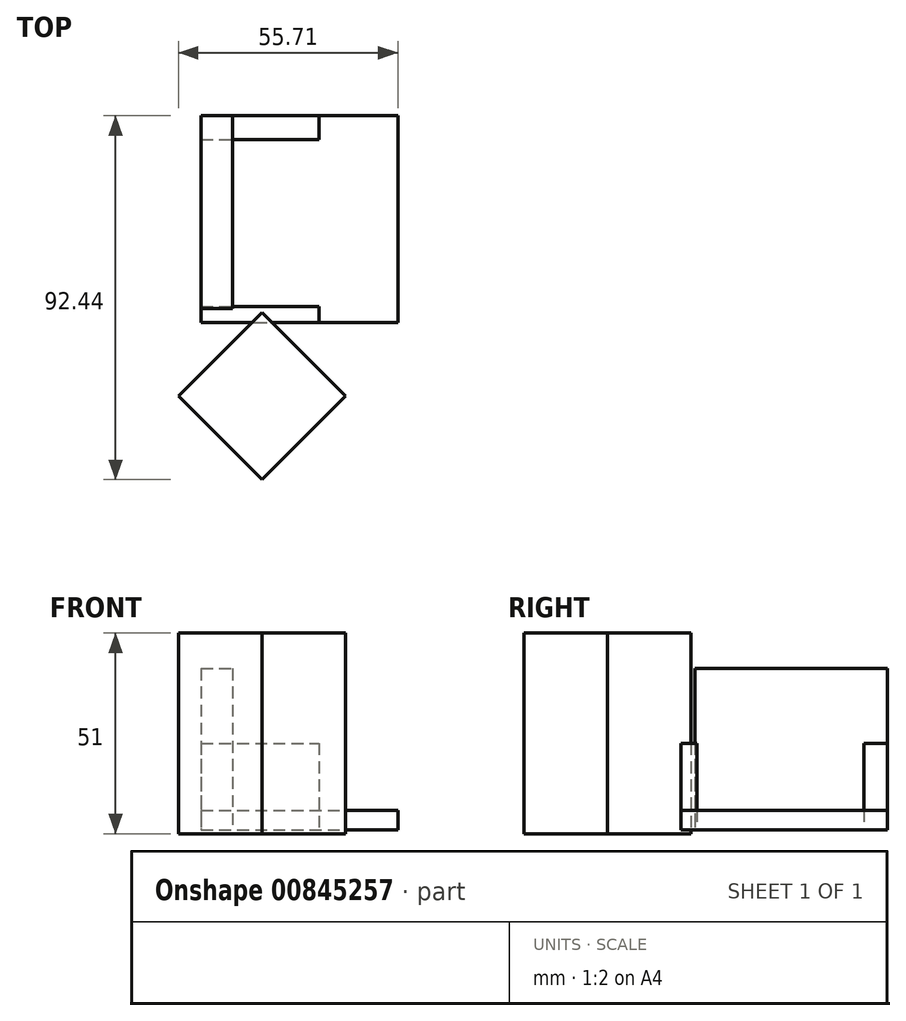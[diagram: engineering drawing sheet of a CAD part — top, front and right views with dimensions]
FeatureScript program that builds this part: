
annotation { "Feature Type Name" : "Feature", "Feature Type Description" : "" }
export const myFeature = defineFeature(function(context is Context, id is Id, definition is map)
    precondition{}
    {
        {
            var Q0;
            Q0=qCreatedBy(makeId("Top.planeOp"),FACE);
            var sketch = newSketch(context, id + "F0", { "sketchPlane" : qUnion([Q0])});
            skLineSegment(sketch, "E0.bottom", {"start": v(0, 0) * mm, "end": v(8, 0) * mm});
            skLineSegment(sketch, "E0.top", {"start": v(0, 49) * mm, "end": v(8, 49) * mm});
            skLineSegment(sketch, "E0.left", {"start": v(0, 0) * mm, "end": v(0, 49) * mm});
            skLineSegment(sketch, "E0.right", {"start": v(8, 0) * mm, "end": v(8, 49) * mm});
            skSolve(sketch);
        }
        {
            var Q0;
            Q0=makeQuery(id+"F0.imprint","IMPRINT",FACE,{"disambiguationData":[TD([[makeQuery(id+"F0.imprint","IMPRINT",EDGE,{"derivedFrom":sQuery(id+"F0.wireOp",EDGE,"E0.bottom")}),1.0]])]});
            extrude(context, id + "F1", {"entities" : qUnion([Q0]), "depth" : (16 + 25) * mm, "offsetDistance" : 25 * mm});
        }
        {
            var Q0;
            Q0=makeQuery(id+"F1.opExtrude","SWEPT_BODY",BODY,{"disambiguationData":[OSD([sQuery(id+"F0.wireOp",EDGE,"E0.bottom"),sQuery(id+"F0.wireOp",EDGE,"E0.top"),sQuery(id+"F0.wireOp",EDGE,"E0.left"),sQuery(id+"F0.wireOp",EDGE,"E0.right")])]});
            transform(context, id + "F2", {"entities" : qUnion([Q0]), "transformType" : TransformType.TRANSLATION_3D, "dx" : 0 * mm, "dy" : -1.5 * mm, "dz" : 0 * mm, "makeCopy" : false});
        }
        {
            var Q0;
            Q0=qCreatedBy(makeId("Top.planeOp"),FACE);
            var sketch = newSketch(context, id + "F3", { "sketchPlane" : qUnion([Q0])});
            skLineSegment(sketch, "E1.bottom", {"start": v(0, 0) * mm, "end": v(30, 0) * mm});
            skLineSegment(sketch, "E1.top", {"start": v(0, 4) * mm, "end": v(30, 4) * mm});
            skLineSegment(sketch, "E1.left", {"start": v(0, 0) * mm, "end": v(0, 4) * mm});
            skLineSegment(sketch, "E1.right", {"start": v(30, 0) * mm, "end": v(30, 4) * mm});
            skSolve(sketch);
        }
        {
            var Q0;
            Q0 = qSketchRegion(id + "F3", true);
            extrude(context, id + "F4", {"entities" : qUnion([Q0]), "depth" : 22 * mm, "offsetDistance" : 25 * mm});
        }
        {
            var Q0;
            Q0=makeQuery(id+"F4.opExtrude","SWEPT_BODY",BODY,{"disambiguationData":[OSD([sQuery(id+"F3.wireOp",EDGE,"E1.bottom"),sQuery(id+"F3.wireOp",EDGE,"E1.top"),sQuery(id+"F3.wireOp",EDGE,"E1.left"),sQuery(id+"F3.wireOp",EDGE,"E1.right")])]});
            transform(context, id + "F5", {"entities" : qUnion([Q0]), "transformType" : TransformType.TRANSLATION_3D, "dx" : 0 * mm, "dy" : -5 * mm, "dz" : 0 * mm, "makeCopy" : false});
        }
        {
            var Q0;
            Q0=qCreatedBy(makeId("Top.planeOp"),FACE);
            var sketch = newSketch(context, id + "F6", { "sketchPlane" : qUnion([Q0])});
            skLineSegment(sketch, "E2.bottom", {"start": v(0, 0) * mm, "end": v(30, 0) * mm});
            skLineSegment(sketch, "E2.top", {"start": v(0, 6.01) * mm, "end": v(30, 6.01) * mm});
            skLineSegment(sketch, "E2.left", {"start": v(0, 0) * mm, "end": v(0, 6.01) * mm});
            skLineSegment(sketch, "E2.right", {"start": v(30, 0) * mm, "end": v(30, 6.01) * mm});
            skSolve(sketch);
        }
        {
            var Q0;
            Q0 = qSketchRegion(id + "F6", true);
            extrude(context, id + "F7", {"entities" : qUnion([Q0]), "depth" : 22 * mm, "offsetDistance" : 25 * mm});
        }
        {
            var Q0;
            Q0=makeQuery(id+"F7.opExtrude","SWEPT_BODY",BODY,{"disambiguationData":[OSD([sQuery(id+"F6.wireOp",EDGE,"E2.bottom"),sQuery(id+"F6.wireOp",EDGE,"E2.top"),sQuery(id+"F6.wireOp",EDGE,"E2.left"),sQuery(id+"F6.wireOp",EDGE,"E2.right")])]});
            transform(context, id + "F8", {"entities" : qUnion([Q0]), "transformType" : TransformType.TRANSLATION_3D, "dx" : 0 * mm, "dy" : 41.5 * mm, "dz" : 0 * mm, "makeCopy" : false});
        }
        {
            var Q0;
            Q0=qCreatedBy(makeId("Top.planeOp"),FACE);
            var sketch = newSketch(context, id + "F9", { "sketchPlane" : qUnion([Q0])});
            skLineSegment(sketch, "E3.bottom", {"start": v(0, 0) * mm, "end": v(50, 0) * mm});
            skLineSegment(sketch, "E3.top", {"start": v(0, 52.5) * mm, "end": v(50, 52.5) * mm});
            skLineSegment(sketch, "E3.left", {"start": v(0, 0) * mm, "end": v(0, 52.5) * mm});
            skLineSegment(sketch, "E3.right", {"start": v(50, 0) * mm, "end": v(50, 52.5) * mm});
            skSolve(sketch);
        }
        {
            var Q0;
            Q0 = qSketchRegion(id + "F9", true);
            extrude(context, id + "F10", {"entities" : qUnion([Q0]), "depth" : 5 * mm, "offsetDistance" : 25 * mm});
        }
        {
            var Q0;
            Q0=makeQuery(id+"F10.opExtrude","SWEPT_BODY",BODY,{"disambiguationData":[OSD([sQuery(id+"F9.wireOp",EDGE,"E3.bottom"),sQuery(id+"F9.wireOp",EDGE,"E3.top"),sQuery(id+"F9.wireOp",EDGE,"E3.left"),sQuery(id+"F9.wireOp",EDGE,"E3.right")])]});
            transform(context, id + "F11", {"entities" : qUnion([Q0]), "transformType" : TransformType.TRANSLATION_3D, "dx" : 0 * mm, "dy" : -5 * mm, "dz" : 0 * mm, "makeCopy" : false});
        }
        {
            var Q0;
            Q0=qCreatedBy(makeId("Top.planeOp"),FACE);
            var sketch = newSketch(context, id + "F12", { "sketchPlane" : qUnion([Q0])});
            skLineSegment(sketch, "E4.bottom", {"start": v(0, 0) * mm, "end": v(30, 0) * mm});
            skLineSegment(sketch, "E4.top", {"start": v(0, 30) * mm, "end": v(30, 30) * mm});
            skLineSegment(sketch, "E4.left", {"start": v(0, 0) * mm, "end": v(0, 30) * mm});
            skLineSegment(sketch, "E4.right", {"start": v(30, 0) * mm, "end": v(30, 30) * mm});
            skSolve(sketch);
        }
        {
            var Q0;
            Q0 = qSketchRegion(id + "F12", true);
            extrude(context, id + "F13", {"entities" : qUnion([Q0]), "depth" : 51 * mm, "offsetDistance" : 25 * mm});
        }
        {
            var Q0;
            Q0=makeQuery(id+"F13.opExtrude","SWEPT_BODY",BODY,{"disambiguationData":[OSD([sQuery(id+"F12.wireOp",EDGE,"E4.bottom"),sQuery(id+"F12.wireOp",EDGE,"E4.top"),sQuery(id+"F12.wireOp",EDGE,"E4.left"),sQuery(id+"F12.wireOp",EDGE,"E4.right")])]});
            transform(context, id + "F14", {"entities" : qUnion([Q0]), "transformType" : TransformType.TRANSLATION_3D, "dx" : -15 * mm, "dy" : 0 * mm, "dz" : -1 * mm, "makeCopy" : false});
        }
        {
            var Q0;
            Q0=qCreatedBy(makeId("Front.planeOp"),FACE);
            var Q1;
            Q1=makeQuery(id+"F13.opExtrude","SWEPT_FACE",FACE,{"disambiguationData":[OSD([sQuery(id+"F12.wireOp",EDGE,"E4.top")])]});
            cPlane(context, id + "F15", {"entities" : qUnion([Q0, Q1]), "cplaneType" : CPlaneType.MID_PLANE, "offset" : 25 * mm, "width" : 150 * mm, "height" : 150 * mm});
        }
        {
            var Q0;
            Q0=makeQuery(id+"F13.opExtrude","SWEPT_BODY",BODY,{"disambiguationData":[OSD([sQuery(id+"F12.wireOp",EDGE,"E4.bottom"),sQuery(id+"F12.wireOp",EDGE,"E4.top"),sQuery(id+"F12.wireOp",EDGE,"E4.left"),sQuery(id+"F12.wireOp",EDGE,"E4.right")])]});
            var Q1;
            Q1=makeQuery(id+"F13.opExtrude","SWEPT_EDGE",EDGE,{"disambiguationData":[OSD([sQuery(id+"F12.wireOp",EDGE,"E4.bottom"),sQuery(id+"F12.wireOp",EDGE,"E4.right")])]});
            transform(context, id + "F16", {"entities" : qUnion([Q0]), "transformType" : TransformType.ROTATION, "transformAxis" : qUnion([Q1]), "angle" : 225 * degree, "makeCopy" : false});
        }
        {
            var Q0;
            Q0=makeQuery(id+"F13.opExtrude","SWEPT_BODY",BODY,{"disambiguationData":[OSD([sQuery(id+"F12.wireOp",EDGE,"E4.bottom"),sQuery(id+"F12.wireOp",EDGE,"E4.top"),sQuery(id+"F12.wireOp",EDGE,"E4.left"),sQuery(id+"F12.wireOp",EDGE,"E4.right")])]});
            transform(context, id + "F17", {"entities" : qUnion([Q0]), "transformType" : TransformType.TRANSLATION_3D, "dx" : 0.5 * mm, "dy" : -2.5 * mm, "dz" : 0 * mm, "makeCopy" : false});
        }
    });
